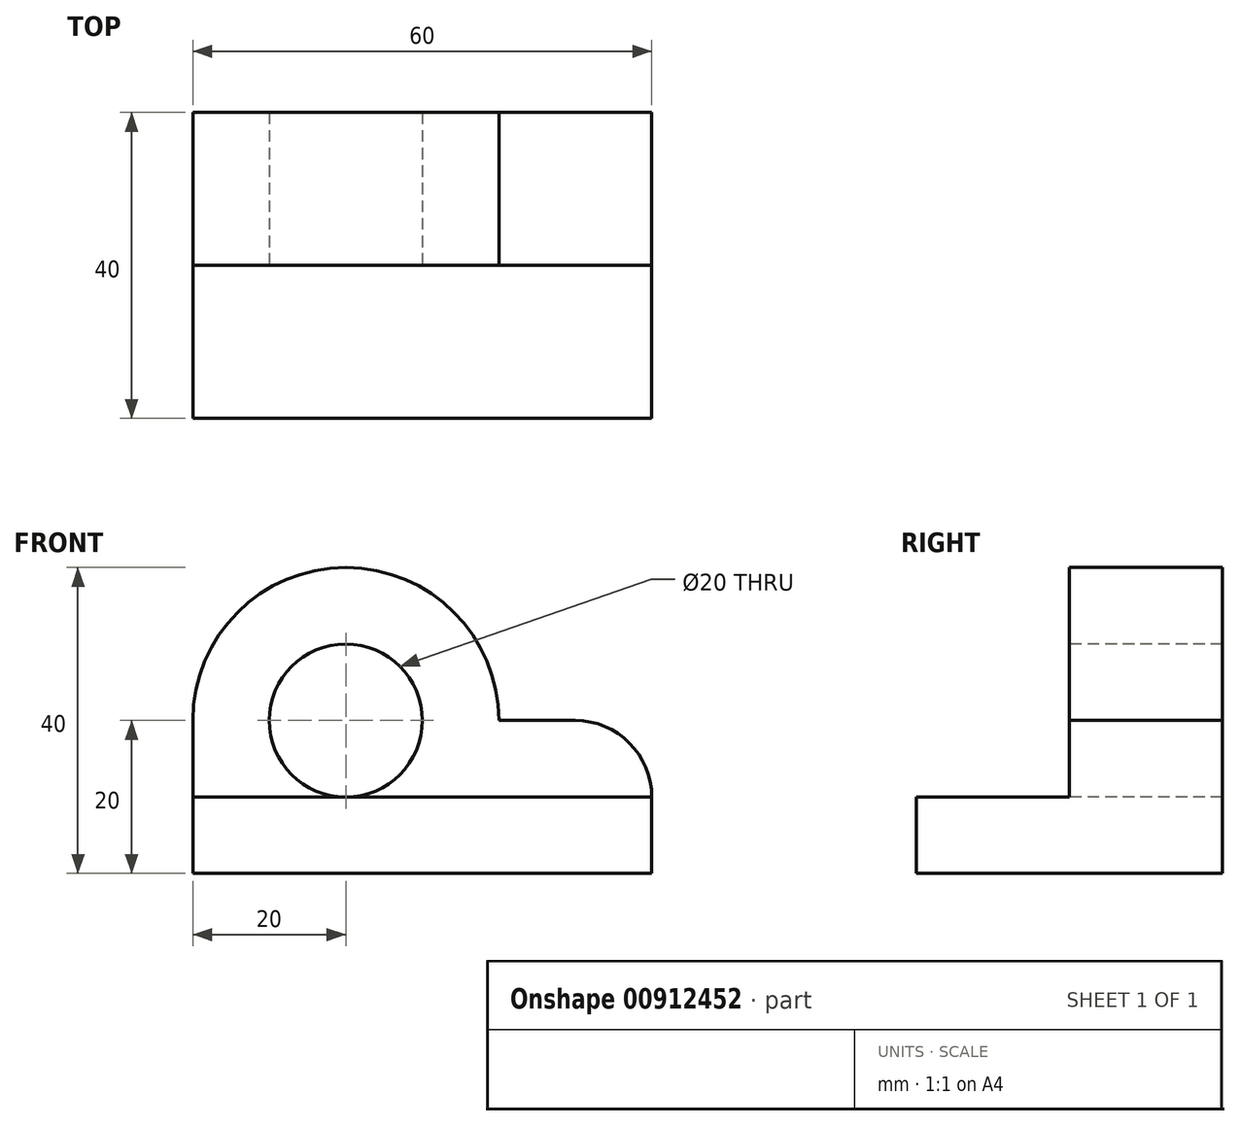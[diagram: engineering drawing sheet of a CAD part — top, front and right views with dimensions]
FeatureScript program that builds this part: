
annotation { "Feature Type Name" : "Feature", "Feature Type Description" : "" }
export const myFeature = defineFeature(function(context is Context, id is Id, definition is map)
    precondition{}
    {
        {
            var Q0;
            Q0=qCreatedBy(makeId("Front.planeOp"),FACE);
            var sketch = newSketch(context, id + "F0", { "sketchPlane" : qUnion([Q0])});
            skLineSegment(sketch, "E0.bottom", {"start": v(0, 0) * mm, "end": v(60, 0) * mm});
            skLineSegment(sketch, "E0.left", {"start": v(0, 0) * mm, "end": v(0, 20) * mm});
            skLineSegment(sketch, "E0.right", {"start": v(60, 0) * mm, "end": v(60, 10) * mm});
            skLineSegment(sketch, "E1", {"start": v(0, 10) * mm, "end": v(60, 10) * mm});
            skLineSegment(sketch, "E2", {"start": v(40, 20) * mm, "end": v(60, 20) * mm, "construction": true});
            skArc(sketch, "E3", {"start": v(40, 20) * mm, "mid": v(20, 40) * mm, "end": v(0, 20) * mm});
            skLineSegment(sketch, "E4", {"start": v(40, 20) * mm, "end": v(50, 20) * mm});
            skPoint(sketch, "E5.orphan", {"position": v(0, 20) * mm});
            skPoint(sketch, "E6.orphan", {"position": v(60, 40) * mm});
            skPoint(sketch, "E7.orphan", {"position": v(0, 40) * mm});
            skPoint(sketch, "E8.visualSharp", {"position": v(60, 20) * mm});
            skArc(sketch, "E8.filletArc", {"start": v(60, 10) * mm, "mid": v(57.07, 17.07) * mm, "end": v(50, 20) * mm});
            skSolve(sketch);
        }
        {
            var Q0;
            {var subQ5=sQuery(id+"F0.wireOp",EDGE,"E0.bottom");Q0=makeQuery(id+"F0.imprint","IMPRINT",FACE,{"disambiguationData":[TD([[makeQuery(id+"F0.imprint","IMPRINT",EDGE,{"derivedFrom":subQ5}),1.0]])]});}
            extrude(context, id + "F1", {"entities" : qUnion([Q0]), "depth" : 40 * mm, "offsetDistance" : 25 * mm});
        }
        {
            var Q0;
            {var subQ1=sQuery(id+"F0.wireOp",EDGE,"E1");Q0=makeQuery(id+"F0.imprint","IMPRINT",FACE,{"disambiguationData":[TD([[makeQuery(id+"F0.imprint","IMPRINT",EDGE,{"derivedFrom":subQ1}),1.0]])]});}
            extrude(context, id + "F2", {"entities" : qUnion([Q0]), "operationType" : NewBodyOperationType.ADD, "depth" : 20 * mm, "offsetDistance" : 25 * mm});
        }
        {
            var Q0;
            Q0=makeQuery(id+"F2.opExtrude","CAP_FACE",FACE,{"disambiguationData":[OSD([sQuery(id+"F0.wireOp",EDGE,"E0.left"),sQuery(id+"F0.wireOp",EDGE,"E1"),sQuery(id+"F0.wireOp",EDGE,"E3"),sQuery(id+"F0.wireOp",EDGE,"E4"),sQuery(id+"F0.wireOp",EDGE,"E8.filletArc")])],"isStart":false});
            var sketch = newSketch(context, id + "F3", { "sketchPlane" : qUnion([Q0])});
            skCircle(sketch, "E9", {"center": v(20, 20) * mm, "radius": 10 * mm});
            skSolve(sketch);
        }
        {
            var Q0;
            Q0=makeQuery(id+"F3.imprint","IMPRINT",FACE,{"disambiguationData":[TD([[makeQuery(id+"F3.imprint","IMPRINT",EDGE,{"derivedFrom":sQuery(id+"F3.wireOp",EDGE,"E9")}),1.0]])]});
            extrude(context, id + "F4", {"entities" : qUnion([Q0]), "operationType" : NewBodyOperationType.REMOVE, "endBound" : BoundingType.THROUGH_ALL, "oppositeDirection" : true, "depth" : 25 * mm, "offsetDistance" : 25 * mm});
        }
    });
